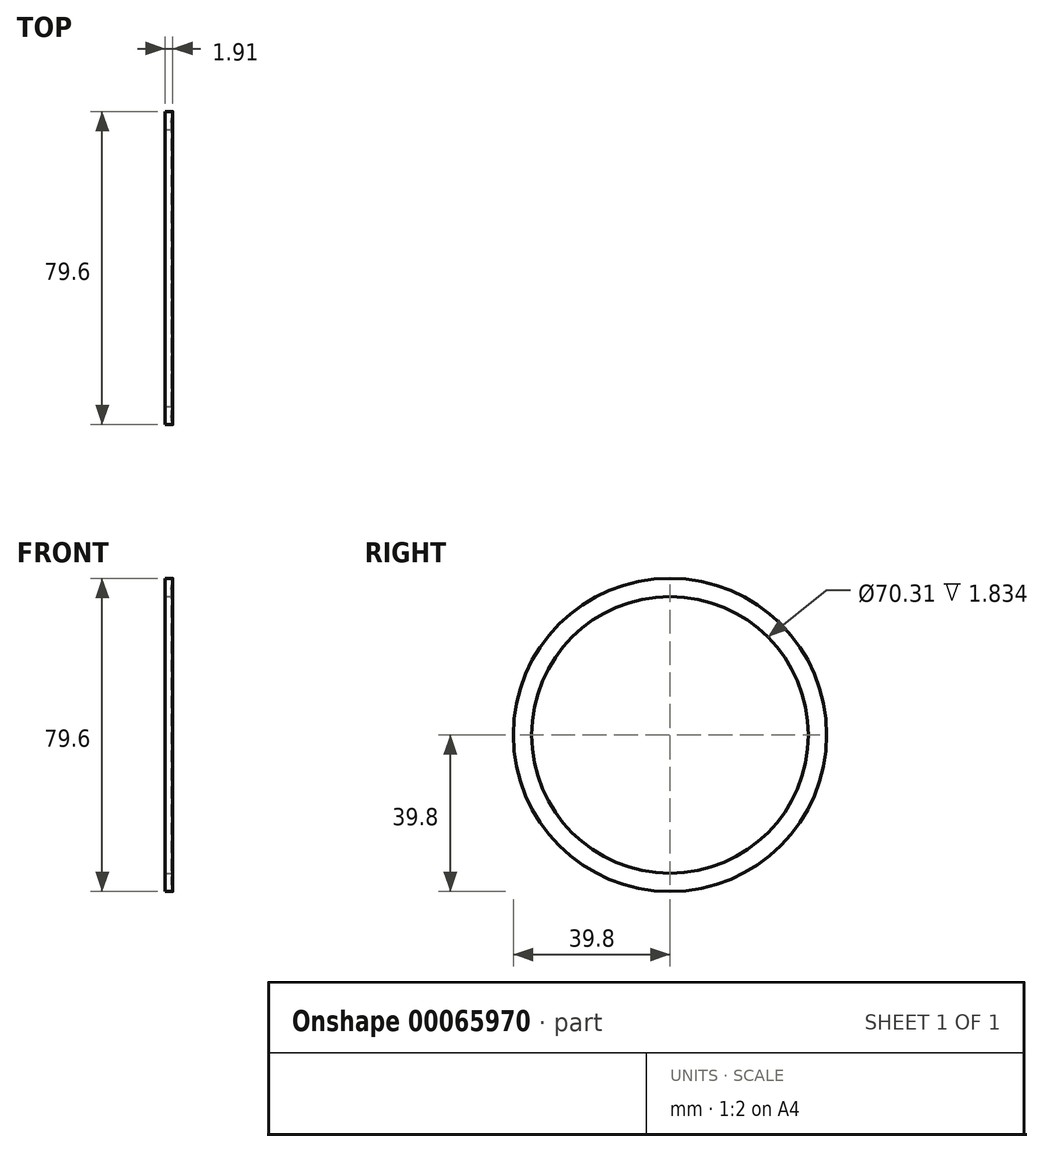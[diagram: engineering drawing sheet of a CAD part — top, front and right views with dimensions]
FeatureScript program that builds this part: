
annotation { "Feature Type Name" : "Feature", "Feature Type Description" : "" }
export const myFeature = defineFeature(function(context is Context, id is Id, definition is map)
    precondition{}
    {
        {
            var Q0;
            Q0=qCreatedBy(makeId("Front.planeOp"),FACE);
            var sketch = newSketch(context, id + "F0", { "sketchPlane" : qUnion([Q0])});
            skLineSegment(sketch, "E0.bottom", {"start": v(-0.1, 39.8) * mm, "end": v(-1.94, 39.8) * mm});
            skLineSegment(sketch, "E0.top", {"start": v(-0.1, 35.15) * mm, "end": v(-1.94, 35.15) * mm});
            skLineSegment(sketch, "E0.right", {"start": v(-1.94, 39.8) * mm, "end": v(-1.94, 35.15) * mm});
            skLineSegment(sketch, "E1", {"start": v(0, 0) * mm, "end": v(-6.16, 0) * mm, "construction": true});
            skArc(sketch, "E2", {"start": v(-0.04, 39.7) * mm, "mid": v(-0.42, 37.48) * mm, "end": v(-0.04, 35.26) * mm});
            skPoint(sketch, "E3.visualSharp", {"position": v(0, 39.8) * mm});
            skArc(sketch, "E3.filletArc", {"start": v(-0.04, 39.7) * mm, "mid": v(-0.05, 39.77) * mm, "end": v(-0.1, 39.8) * mm});
            skPoint(sketch, "E4.visualSharp", {"position": v(0, 35.15) * mm});
            skArc(sketch, "E4.filletArc", {"start": v(-0.1, 35.15) * mm, "mid": v(-0.05, 35.19) * mm, "end": v(-0.04, 35.26) * mm});
            skLineSegment(sketch, "E5", {"start": v(0, 35.15) * mm, "end": v(0, 0) * mm, "construction": true});
            skSolve(sketch);
        }
        {
            var Q0;
            Q0=makeQuery(id+"F0.imprint","IMPRINT",FACE,{"disambiguationData":[TD([[makeQuery(id+"F0.imprint","IMPRINT",EDGE,{"derivedFrom":sQuery(id+"F0.wireOp",EDGE,"E0.bottom")}),1.0]])]});
            var Q1;
            Q1=sQuery(id+"F0.wireOp",EDGE,"E1");
            revolve(context, id + "F1", {"entities" : qUnion([Q0]), "axis" : qUnion([Q1]), "revolveType" : RevolveType.FULL});
        }
    });
